FCSTD DOCUMENT  (FreeCAD 0.21R33668 +7 (Git))
Label: reference-measurements
License: All rights reserved
LicenseURL: http://en.wikipedia.org/wiki/All_rights_reserved
objects: Image::ImagePlane×1, Sketcher::SketchObject×1, PartDesign::Body×1
note: 2 computed .brp shape members not serialized (recipe doc carries the construction recipe); baked Part::Feature solids carry a one-line shape summary decoded from their .brp

FEATURE [Image::ImagePlane] ImagePlane  label="Back Side"
  Placement = pos=(0.93345,0,0) rot=(0,0,-1;0.00384rad)
  XSize = 173.699
  YSize = 101.777
FEATURE [Sketcher::SketchObject] Sketch
  FullyConstrained = false
  MapMode = 5
  Support = -> [XY_Plane]
  sketch-geometry (50):
    g0: GeomPoint X=-74.11 Y=-11.5086 Z=0
    g1: GeomPoint X=74.11 Y=-11.5603 Z=0
    g2: Circle CenterX=-7.80263 CenterY=-40.5201 CenterZ=0 NormalX=0 NormalY=0 NormalZ=1 AngleXU=0 Radius=1.10105
    g3: Circle CenterX=7.8245 CenterY=-40.5399 CenterZ=0 NormalX=0 NormalY=0 NormalZ=1 AngleXU=0 Radius=1.23952
    g4: LineSegment StartX=-46.6 StartY=-10.43 StartZ=0 EndX=-46.6 EndY=-21.63 EndZ=0
    g5: LineSegment StartX=-46.6 StartY=-21.63 StartZ=0 EndX=-38.4 EndY=-21.63 EndZ=0
    g6: LineSegment StartX=-38.4 StartY=-21.63 StartZ=0 EndX=-38.4 EndY=-10.43 EndZ=0
    g7: LineSegment StartX=-38.4 StartY=-10.43 StartZ=0 EndX=-46.6 EndY=-10.43 EndZ=0
    g8: GeomPoint X=-42.5 Y=-16.03 Z=0
    g9: LineSegment StartX=-68.1 StartY=-8.93 StartZ=0 EndX=-68.1 EndY=-17.13 EndZ=0
    g10: LineSegment StartX=-68.1 StartY=-17.13 StartZ=0 EndX=-56.9 EndY=-17.13 EndZ=0
    g11: LineSegment StartX=-56.9 StartY=-17.13 StartZ=0 EndX=-56.9 EndY=-8.93 EndZ=0
    g12: LineSegment StartX=-56.9 StartY=-8.93 StartZ=0 EndX=-68.1 EndY=-8.93 EndZ=0
    g13: GeomPoint X=-62.5 Y=-13.03 Z=0
    g14: LineSegment StartX=-54.6 StartY=9.57 StartZ=0 EndX=-54.6 EndY=1.37 EndZ=0
    g15: LineSegment StartX=-54.6 StartY=1.37 StartZ=0 EndX=-43.4 EndY=1.37 EndZ=0
    g16: LineSegment StartX=-43.4 StartY=1.37 StartZ=0 EndX=-43.4 EndY=9.57 EndZ=0
    g17: LineSegment StartX=-43.4 StartY=9.57 StartZ=0 EndX=-54.6 EndY=9.57 EndZ=0
    g18: GeomPoint X=-49 Y=5.47 Z=0
    g19: LineSegment StartX=-33.1 StartY=6.77 StartZ=0 EndX=-33.1 EndY=-1.43 EndZ=0
    g20: LineSegment StartX=-33.1 StartY=-1.43 StartZ=0 EndX=-21.9 EndY=-1.43 EndZ=0
    g21: LineSegment StartX=-21.9 StartY=-1.43 StartZ=0 EndX=-21.9 EndY=6.77 EndZ=0
    g22: LineSegment StartX=-21.9 StartY=6.77 StartZ=0 EndX=-33.1 EndY=6.77 EndZ=0
    g23: GeomPoint X=-27.5 Y=2.67 Z=0
    g24: LineSegment StartX=33.1 StartY=6.77 StartZ=0 EndX=33.1 EndY=-1.43 EndZ=0
    g25: LineSegment StartX=33.1 StartY=-1.43 StartZ=0 EndX=21.9 EndY=-1.43 EndZ=0
    g26: LineSegment StartX=21.9 StartY=-1.43 StartZ=0 EndX=21.9 EndY=6.77 EndZ=0
    g27: LineSegment StartX=21.9 StartY=6.77 StartZ=0 EndX=33.1 EndY=6.77 EndZ=0
    g28: GeomPoint X=27.5 Y=2.67 Z=0
    g29: LineSegment StartX=38.4 StartY=-10.43 StartZ=0 EndX=38.4 EndY=-21.63 EndZ=0
    g30: LineSegment StartX=38.4 StartY=-21.63 StartZ=0 EndX=46.6 EndY=-21.63 EndZ=0
    g31: LineSegment StartX=46.6 StartY=-21.63 StartZ=0 EndX=46.6 EndY=-10.43 EndZ=0
    g32: LineSegment StartX=46.6 StartY=-10.43 StartZ=0 EndX=38.4 EndY=-10.43 EndZ=0
    g33: GeomPoint X=42.5 Y=-16.03 Z=0
    g34: LineSegment StartX=68.1 StartY=-8.93 StartZ=0 EndX=68.1 EndY=-17.13 EndZ=0
    g35: LineSegment StartX=68.1 StartY=-17.13 StartZ=0 EndX=56.9 EndY=-17.13 EndZ=0
    g36: LineSegment StartX=56.9 StartY=-17.13 StartZ=0 EndX=56.9 EndY=-8.93 EndZ=0
    g37: LineSegment StartX=56.9 StartY=-8.93 StartZ=0 EndX=68.1 EndY=-8.93 EndZ=0
    g38: GeomPoint X=62.5 Y=-13.03 Z=0
    g39: LineSegment StartX=54.6 StartY=9.57 StartZ=0 EndX=54.6 EndY=1.37 EndZ=0
    g40: LineSegment StartX=54.6 StartY=1.37 StartZ=0 EndX=43.4 EndY=1.37 EndZ=0
    g41: LineSegment StartX=43.4 StartY=1.37 StartZ=0 EndX=43.4 EndY=9.57 EndZ=0
    g42: LineSegment StartX=43.4 StartY=9.57 StartZ=0 EndX=54.6 EndY=9.57 EndZ=0
    g43: GeomPoint X=49 Y=5.47 Z=0
    g44: Circle CenterX=-2.59358 CenterY=-40.5267 CenterZ=0 NormalX=0 NormalY=0 NormalZ=1 AngleXU=0 Radius=1.04633
    g45: Circle CenterX=2.61546 CenterY=-40.5333 CenterZ=0 NormalX=0 NormalY=0 NormalZ=1 AngleXU=0 Radius=1.06754
    g46: LineSegment StartX=-7.80263 StartY=-40.5201 StartZ=0 EndX=-2.59358 EndY=-40.5267 EndZ=0
    g47: LineSegment StartX=-2.59358 StartY=-40.5267 StartZ=0 EndX=2.61546 EndY=-40.5333 EndZ=0
    g48: LineSegment StartX=2.61546 StartY=-40.5333 StartZ=0 EndX=7.8245 EndY=-40.5399 EndZ=0
    g49: GeomPoint X=0 Y=-40.53 Z=0
  constraints (120):
    c: Distance(g0,g-2) = 74.11
    c: Distance(g1,g-2) = 74.11
    c: Distance(g2,g3) = 15.6271
    c: Coincident(g4,g5)
    c: Coincident(g5,g6)
    c: Coincident(g6,g7)
    c: Coincident(g7,g4)
    c: Horizontal(g5)
    c: Horizontal(g7)
    c: Vertical(g4)
    c: Vertical(g6)
    c: Symmetric(g5,g4,g8)
    c: Coincident(g9,g10)
    c: Coincident(g10,g11)
    c: Coincident(g11,g12)
    c: Coincident(g12,g9)
    c: Horizontal(g10)
    c: Horizontal(g12)
    c: Vertical(g9)
    c: Vertical(g11)
    c: Symmetric(g10,g9,g13)
    c: Coincident(g14,g15)
    c: Coincident(g15,g16)
    c: Coincident(g16,g17)
    c: Coincident(g17,g14)
    c: Horizontal(g15)
    c: Horizontal(g17)
    c: Vertical(g14)
    c: Vertical(g16)
    c: Symmetric(g15,g14,g18)
    c: Coincident(g19,g20)
    c: Coincident(g20,g21)
    c: Coincident(g21,g22)
    c: Coincident(g22,g19)
    c: Horizontal(g20)
    c: Horizontal(g22)
    c: Vertical(g19)
    c: Vertical(g21)
    c: Symmetric(g20,g19,g23)
    c: Coincident(g24,g25)
    c: Coincident(g25,g26)
    c: Coincident(g26,g27)
    c: Coincident(g27,g24)
    c: Horizontal(g25)
    c: Horizontal(g27)
    c: Vertical(g24)
    c: Vertical(g26)
    c: Symmetric(g25,g24,g28)
    c: Coincident(g29,g30)
    c: Coincident(g30,g31)
    c: Coincident(g31,g32)
    c: Coincident(g32,g29)
    c: Horizontal(g30)
    c: Horizontal(g32)
    c: Vertical(g29)
    c: Vertical(g31)
    c: Symmetric(g30,g29,g33)
    c: Coincident(g34,g35)
    c: Coincident(g35,g36)
    c: Coincident(g36,g37)
    c: Coincident(g37,g34)
    c: Horizontal(g35)
    c: Horizontal(g37)
    c: Vertical(g34)
    c: Vertical(g36)
    c: Symmetric(g35,g34,g38)
    c: Coincident(g39,g40)
    c: Coincident(g40,g41)
    c: Coincident(g41,g42)
    c: Coincident(g42,g39)
    c: Horizontal(g40)
    c: Horizontal(g42)
    c: Vertical(g39)
    c: Vertical(g41)
    c: Symmetric(g40,g39,g43)
    c: Coincident(g46,g2)
    c: Coincident(g46,g44)
    c: Coincident(g47,g44)
    c: Coincident(g47,g45)
    c: Coincident(g48,g45)
    c: Coincident(g48,g3)
    c: PointOnObject(g45,g46)
    c: PointOnObject(g3,g46)
    c: Equal(g46,g47)
    c: Equal(g47,g48)
    c: Distance(g46) = 5.20905
    c: Distance(g47) = 5.20905
    c: Distance(g48) = 5.20905
    c: PointOnObject(g49,g47)
    c: PointOnObject(g49,g-2)
    c: DistanceX(g8,g49) = 42.5
    c: DistanceX(g13,g49) = 62.5
    c: DistanceX(g23,g49) = 27.5
    c: DistanceX(g18,g49) = 49
    c: DistanceY(g49,g8) = 24.5
    c: DistanceY(g49,g13) = 27.5
    c: DistanceY(g49,g23) = 43.2
    c: DistanceY(g49,g18) = 46
    c: Symmetric(g18,g43,g-2)
    c: Symmetric(g23,g28,g-2)
    c: Equal(g7,g11)
    c: Equal(g11,g16)
    c: Equal(g16,g19)
    c: Equal(g19,g24)
    c: Equal(g24,g41)
    c: Equal(g41,g36)
    c: Equal(g36,g32)
    c: Equal(g12,g20)
    c: Equal(g20,g4)
    c: Equal(g4,g25)
    c: Equal(g25,g40)
    c: Equal(g40,g37)
    c: Equal(g37,g31)
    c: Distance(g16) = 8.2
    c: Distance(g-1,g49) = 40.53  'Lock'
    c: Equal(g12,g15)
    c: Distance(g15) = 11.2
    c: Symmetric(g33,g8,g-2)
    c: Symmetric(g38,g13,g-2)
    c: Distance(g0,g1) = 148.22
FEATURE [PartDesign::Body] Body
  Group = -> [Sketch]
  Origin = -> Origin
